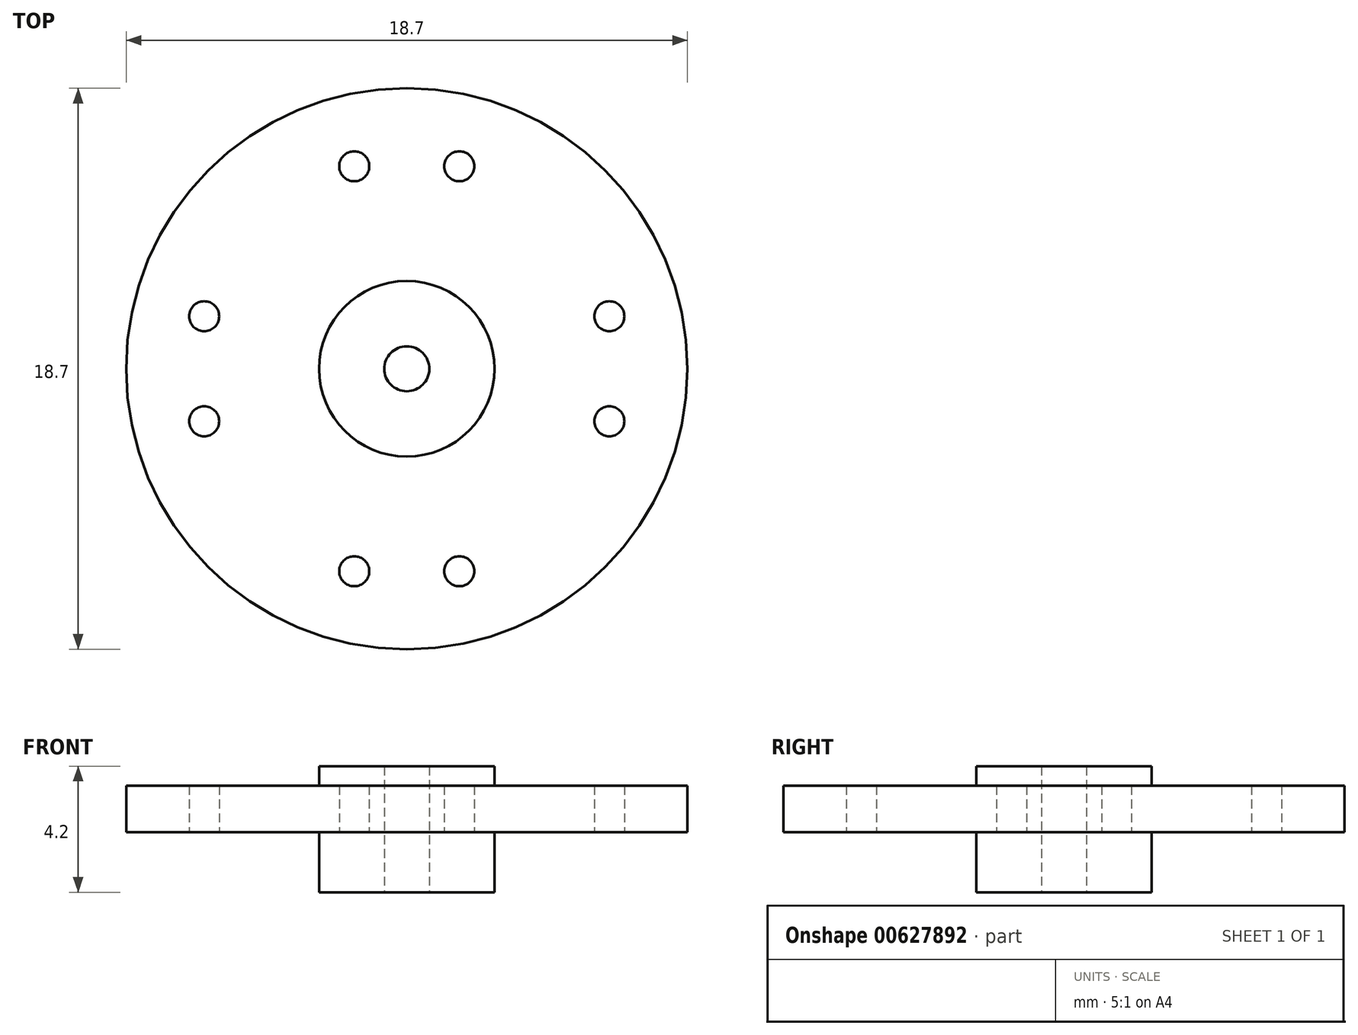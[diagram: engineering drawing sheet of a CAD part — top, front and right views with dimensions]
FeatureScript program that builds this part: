
annotation { "Feature Type Name" : "Feature", "Feature Type Description" : "" }
export const myFeature = defineFeature(function(context is Context, id is Id, definition is map)
    precondition{}
    {
        {
            var Q0;
            Q0=qCreatedBy(makeId("Top.planeOp"),FACE);
            var sketch = newSketch(context, id + "F0", { "sketchPlane" : qUnion([Q0])});
            skLineSegment(sketch, "E0", {"start": v(0, 0) * mm, "end": v(0, 24.29) * mm, "construction": true});
            skCircle(sketch, "E1", {"center": v(0, 0) * mm, "radius": 2.93 * mm});
            skCircle(sketch, "E2", {"center": v(0, 0) * mm, "radius": 0.75 * mm});
            skCircle(sketch, "E3", {"center": v(0, 0) * mm, "radius": 9.35 * mm});
            skLineSegment(sketch, "E4", {"start": v(0, 0) * mm, "end": v(20.1, 0) * mm, "construction": true});
            skCircle(sketch, "E5", {"center": v(1.75, 6.75) * mm, "radius": 0.5 * mm});
            skCircle(sketch, "E6.MirrorC", {"center": v(-1.75, 6.75) * mm, "radius": 0.5 * mm});
            skCircle(sketch, "E7", {"center": v(6.75, 1.75) * mm, "radius": 0.5 * mm});
            skCircle(sketch, "E8.MirrorC", {"center": v(6.75, -1.75) * mm, "radius": 0.5 * mm});
            skCircle(sketch, "E9.MirrorC", {"center": v(-6.75, 1.75) * mm, "radius": 0.5 * mm});
            skCircle(sketch, "E10.MirrorC", {"center": v(-6.75, -1.75) * mm, "radius": 0.5 * mm});
            skCircle(sketch, "E11.MirrorC", {"center": v(1.75, -6.75) * mm, "radius": 0.5 * mm});
            skCircle(sketch, "E12.MirrorC", {"center": v(-1.75, -6.75) * mm, "radius": 0.5 * mm});
            skSolve(sketch);
        }
        {
            var Q0;
            Q0=qSketchRegion(id+"F0",true);
            var Q1;
            Q1=makeQuery(id+"F0.imprint","IMPRINT",FACE,{"disambiguationData":[TD([[makeQuery(id+"F0.imprint","IMPRINT",EDGE,{"derivedFrom":sQuery(id+"F0.wireOp",EDGE,"E1")}),1.0]])]});
            extrude(context, id + "F1", {"entities" : qUnion([Q0, Q1]), "depth" : 1.55 * mm, "offsetDistance" : 25 * mm});
        }
        {
            var Q0;
            Q0=makeQuery(id+"F1.opExtrude","CAP_FACE",FACE,{"disambiguationData":[OSD([sQuery(id+"F0.wireOp",EDGE,"E2"),sQuery(id+"F0.wireOp",EDGE,"E3")])],"isStart":true});
            var sketch = newSketch(context, id + "F2", { "sketchPlane" : qUnion([Q0])});
            skCircle(sketch, "E13.0", {"center": v(0, 0) * mm, "radius": 2.93 * mm});
            skCircle(sketch, "E14.0", {"center": v(0, 0) * mm, "radius": 0.75 * mm});
            skSolve(sketch);
        }
        {
            var Q0;
            Q0=qSketchRegion(id+"F2",true);
            extrude(context, id + "F3", {"entities" : qUnion([Q0]), "operationType" : NewBodyOperationType.ADD, "depth" : 2 * mm, "offsetDistance" : 25 * mm, "hasSecondDirection" : true, "secondDirectionOppositeDirection" : true, "secondDirectionDepth" : 2.2 * mm});
        }
    });
